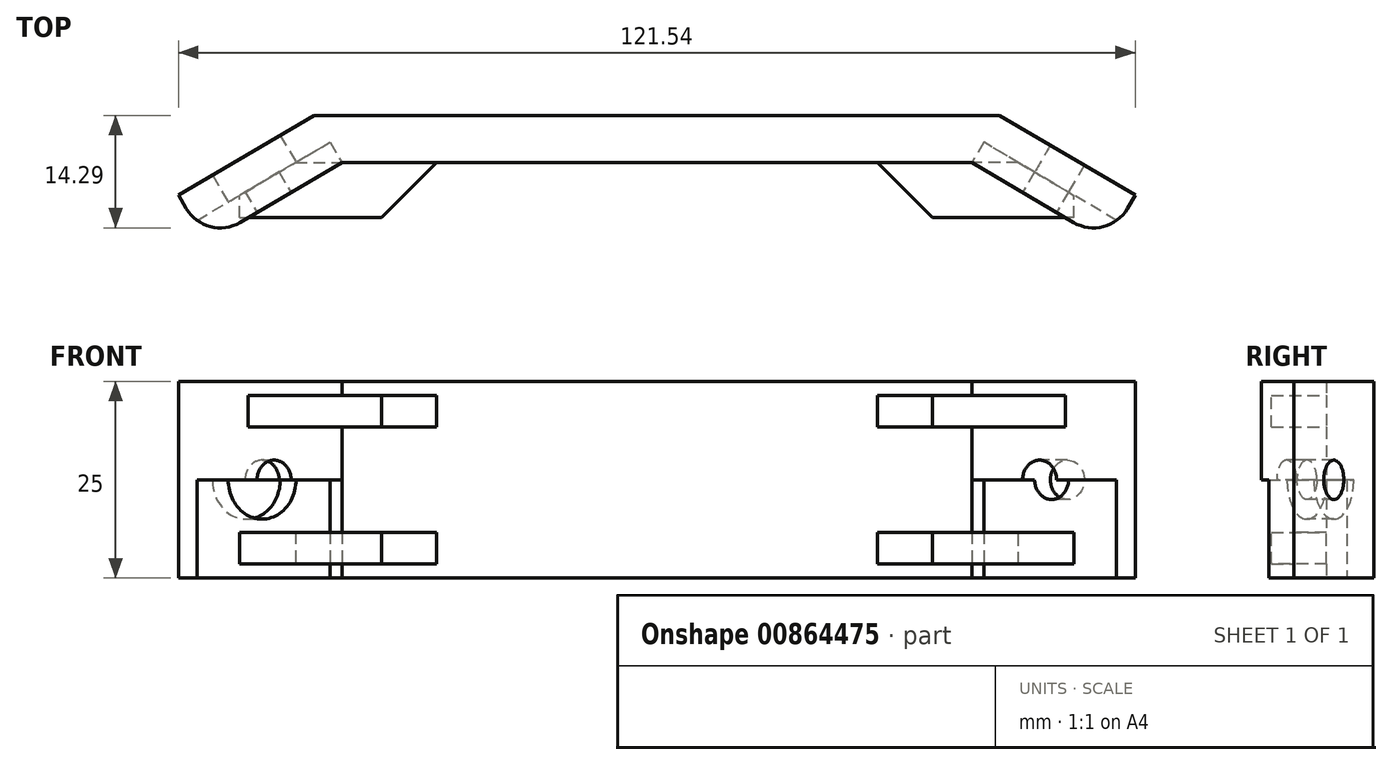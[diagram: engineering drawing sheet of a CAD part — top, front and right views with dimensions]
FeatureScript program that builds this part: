
annotation { "Feature Type Name" : "Feature", "Feature Type Description" : "" }
export const myFeature = defineFeature(function(context is Context, id is Id, definition is map)
    precondition{}
    {
        {
            var Q0;
            Q0=qCreatedBy(makeId("Top.planeOp"),FACE);
            var sketch = newSketch(context, id + "F0", { "sketchPlane" : qUnion([Q0])});
            skLineSegment(sketch, "E0", {"start": v(-33.18, 0) * mm, "end": v(46.82, 0) * mm});
            skLineSegment(sketch, "E1", {"start": v(46.82, 0) * mm, "end": v(46.82, -6) * mm});
            skLineSegment(sketch, "E2", {"start": v(46.82, -6) * mm, "end": v(-33.18, -6) * mm});
            skLineSegment(sketch, "E3", {"start": v(-33.18, -6) * mm, "end": v(-33.18, 0) * mm});
            skLineSegment(sketch, "E4", {"start": v(-33.18, -6) * mm, "end": v(-36.7, 0) * mm});
            skLineSegment(sketch, "E5", {"start": v(-33.18, 0) * mm, "end": v(-36.7, 0) * mm});
            skLineSegment(sketch, "E6", {"start": v(46.82, 0) * mm, "end": v(50.35, 0) * mm});
            skLineSegment(sketch, "E7", {"start": v(50.35, 0) * mm, "end": v(46.82, -6) * mm});
            skLineSegment(sketch, "E8", {"start": v(-36.7, 0) * mm, "end": v(-53.95, -10.14) * mm});
            skLineSegment(sketch, "E9", {"start": v(-53.95, -10.14) * mm, "end": v(-50.42, -16.14) * mm});
            skLineSegment(sketch, "E10", {"start": v(-50.42, -16.14) * mm, "end": v(-33.18, -6) * mm});
            skLineSegment(sketch, "E11", {"start": v(-33.18, 0) * mm, "end": v(6.82, 0) * mm});
            skLineSegment(sketch, "E12", {"start": v(50.35, 0) * mm, "end": v(67.59, -10.14) * mm});
            skLineSegment(sketch, "E13", {"start": v(67.59, -10.14) * mm, "end": v(64.06, -16.14) * mm});
            skLineSegment(sketch, "E14", {"start": v(64.06, -16.14) * mm, "end": v(46.82, -6) * mm});
            skSolve(sketch);
        }
        {
            var Q0;
            Q0=makeQuery(id+"F0.imprint","IMPRINT",FACE,{"disambiguationData":[TD([[makeQuery(id+"F0.imprint","IMPRINT",EDGE,{"derivedFrom":sQuery(id+"F0.wireOp",EDGE,"E4")}),1.0]])]});
            var Q1;
            Q1=makeQuery(id+"F0.imprint","IMPRINT",FACE,{"disambiguationData":[TD([[makeQuery(id+"F0.imprint","IMPRINT",EDGE,{"derivedFrom":sQuery(id+"F0.wireOp",EDGE,"E3")}),1.0]])]});
            var Q2;
            Q2=makeQuery(id+"F0.imprint","IMPRINT",FACE,{"disambiguationData":[TD([[makeQuery(id+"F0.imprint","IMPRINT",EDGE,{"derivedFrom":sQuery(id+"F0.wireOp",EDGE,"E0")}),-1.0]])]});
            var Q3;
            Q3=makeQuery(id+"F0.imprint","IMPRINT",FACE,{"disambiguationData":[TD([[makeQuery(id+"F0.imprint","IMPRINT",EDGE,{"derivedFrom":sQuery(id+"F0.wireOp",EDGE,"E1")}),1.0]])]});
            var Q4;
            Q4=makeQuery(id+"F0.imprint","IMPRINT",FACE,{"disambiguationData":[TD([[makeQuery(id+"F0.imprint","IMPRINT",EDGE,{"derivedFrom":sQuery(id+"F0.wireOp",EDGE,"E7")}),1.0]])]});
            extrude(context, id + "F1", {"entities" : qUnion([Q0, Q1, Q2, Q3, Q4]), "depth" : 25 * mm, "offsetDistance" : 25 * mm});
        }
        {
            var Q0;
            Q0=makeQuery(id+"F1.opExtrude","SWEPT_FACE",FACE,{"disambiguationData":[OSD([sQuery(id+"F0.wireOp",EDGE,"E10")])]});
            var sketch = newSketch(context, id + "F2", { "sketchPlane" : qUnion([Q0])});
            skLineSegment(sketch, "E15", {"start": v(-41.65, 25) * mm, "end": v(-41.65, 0) * mm});
            skLineSegment(sketch, "E16", {"start": v(-51.65, 12.5) * mm, "end": v(-31.65, 12.5) * mm});
            skCircle(sketch, "E17", {"center": v(-41.65, 12.5) * mm, "radius": 5 * mm});
            skCircle(sketch, "E18", {"center": v(-41.65, 12.5) * mm, "radius": 2.5 * mm});
            skSolve(sketch);
        }
        {
            var Q0;
            {var subQ0=sQuery(id+"F2.wireOp",EDGE,"E16");var subQ1=sQuery(id+"F2.wireOp",EDGE,"E15");var subQ2=makeQuery(id+"F2.imprint","INTERSECT",VERTEX,{"derivedFrom":[subQ1,subQ0]});Q0=makeQuery(id+"F2.imprint","IMPRINT",FACE,{"disambiguationData":[TD([[makeQuery(id+"F2.imprint","IMPRINT",EDGE,{"disambiguationData":[TD([[subQ2,-1.0]])],"derivedFrom":subQ1}),-1.0]])]});}
            var Q1;
            {var subQ0=sQuery(id+"F2.wireOp",EDGE,"E16");var subQ1=sQuery(id+"F2.wireOp",EDGE,"E15");var subQ2=makeQuery(id+"F2.imprint","INTERSECT",VERTEX,{"derivedFrom":[subQ1,subQ0]});Q1=makeQuery(id+"F2.imprint","IMPRINT",FACE,{"disambiguationData":[TD([[makeQuery(id+"F2.imprint","IMPRINT",EDGE,{"disambiguationData":[TD([[subQ2,-1.0]])],"derivedFrom":subQ1}),1.0]])]});}
            var Q2;
            {var subQ0=sQuery(id+"F2.wireOp",EDGE,"E18");var subQ1=sQuery(id+"F2.wireOp",EDGE,"E15");var subQ2=makeQuery(id+"F2.imprint","INTERSECT",VERTEX,{"disambiguationData":[OD(0.0)],"derivedFrom":[subQ1,subQ0]});Q2=makeQuery(id+"F2.imprint","IMPRINT",FACE,{"disambiguationData":[TD([[makeQuery(id+"F2.imprint","IMPRINT",EDGE,{"disambiguationData":[TD([[subQ2,-1.0]])],"derivedFrom":subQ1}),1.0]])]});}
            var Q3;
            {var subQ0=sQuery(id+"F2.wireOp",EDGE,"E18");var subQ1=sQuery(id+"F2.wireOp",EDGE,"E15");var subQ2=makeQuery(id+"F2.imprint","INTERSECT",VERTEX,{"disambiguationData":[OD(0.0)],"derivedFrom":[subQ1,subQ0]});Q3=makeQuery(id+"F2.imprint","IMPRINT",FACE,{"disambiguationData":[TD([[makeQuery(id+"F2.imprint","IMPRINT",EDGE,{"disambiguationData":[TD([[subQ2,-1.0]])],"derivedFrom":subQ1}),-1.0]])]});}
            extrude(context, id + "F3", {"entities" : qUnion([Q0, Q1, Q2, Q3]), "operationType" : NewBodyOperationType.REMOVE, "oppositeDirection" : true, "depth" : 25 * mm, "offsetDistance" : 25 * mm});
        }
        {
            var Q0;
            {var subQ0=sQuery(id+"F2.wireOp",EDGE,"E17");var subQ1=sQuery(id+"F2.wireOp",EDGE,"E15");var subQ2=makeQuery(id+"F2.imprint","INTERSECT",VERTEX,{"disambiguationData":[OD(0.0)],"derivedFrom":[subQ1,subQ0]});Q0=makeQuery(id+"F2.imprint","IMPRINT",FACE,{"disambiguationData":[TD([[makeQuery(id+"F2.imprint","IMPRINT",EDGE,{"disambiguationData":[TD([[subQ2,-1.0]])],"derivedFrom":subQ1}),-1.0]])]});}
            var Q1;
            {var subQ0=sQuery(id+"F2.wireOp",EDGE,"E18");var subQ1=sQuery(id+"F2.wireOp",EDGE,"E15");var subQ2=makeQuery(id+"F2.imprint","INTERSECT",VERTEX,{"disambiguationData":[OD(1.0)],"derivedFrom":[subQ1,subQ0]});Q1=makeQuery(id+"F2.imprint","IMPRINT",FACE,{"disambiguationData":[TD([[makeQuery(id+"F2.imprint","IMPRINT",EDGE,{"disambiguationData":[TD([[subQ2,-1.0]])],"derivedFrom":subQ1}),-1.0]])]});}
            var Q2;
            {var subQ0=sQuery(id+"F2.wireOp",EDGE,"E18");var subQ1=sQuery(id+"F2.wireOp",EDGE,"E15");var subQ2=makeQuery(id+"F2.imprint","INTERSECT",VERTEX,{"disambiguationData":[OD(1.0)],"derivedFrom":[subQ1,subQ0]});Q2=makeQuery(id+"F2.imprint","IMPRINT",FACE,{"disambiguationData":[TD([[makeQuery(id+"F2.imprint","IMPRINT",EDGE,{"disambiguationData":[TD([[subQ2,-1.0]])],"derivedFrom":subQ1}),1.0]])]});}
            var Q3;
            {var subQ0=sQuery(id+"F2.wireOp",EDGE,"E17");var subQ1=sQuery(id+"F2.wireOp",EDGE,"E15");var subQ2=makeQuery(id+"F2.imprint","INTERSECT",VERTEX,{"disambiguationData":[OD(0.0)],"derivedFrom":[subQ1,subQ0]});Q3=makeQuery(id+"F2.imprint","IMPRINT",FACE,{"disambiguationData":[TD([[makeQuery(id+"F2.imprint","IMPRINT",EDGE,{"disambiguationData":[TD([[subQ2,-1.0]])],"derivedFrom":subQ1}),1.0]])]});}
            extrude(context, id + "F4", {"entities" : qUnion([Q0, Q1, Q2, Q3]), "operationType" : NewBodyOperationType.REMOVE, "oppositeDirection" : true, "depth" : 3 * mm, "offsetDistance" : 25 * mm});
        }
        {
            var Q0;
            Q0=makeQuery(id+"F1.opExtrude","SWEPT_FACE",FACE,{"disambiguationData":[OSD([sQuery(id+"F0.wireOp",EDGE,"E14")])]});
            var sketch = newSketch(context, id + "F5", { "sketchPlane" : qUnion([Q0])});
            skLineSegment(sketch, "E19", {"start": v(53.4, 25) * mm, "end": v(53.4, 0) * mm});
            skLineSegment(sketch, "E20", {"start": v(63.4, 12.5) * mm, "end": v(43.4, 12.5) * mm});
            skCircle(sketch, "E21", {"center": v(53.4, 12.5) * mm, "radius": 5 * mm});
            skCircle(sketch, "E22", {"center": v(53.4, 12.5) * mm, "radius": 2.5 * mm});
            skSolve(sketch);
        }
        {
            var Q0;
            {var subQ0=sQuery(id+"F5.wireOp",EDGE,"E20");var subQ1=sQuery(id+"F5.wireOp",EDGE,"E19");var subQ2=makeQuery(id+"F5.imprint","INTERSECT",VERTEX,{"derivedFrom":[subQ1,subQ0]});Q0=makeQuery(id+"F5.imprint","IMPRINT",FACE,{"disambiguationData":[TD([[makeQuery(id+"F5.imprint","IMPRINT",EDGE,{"disambiguationData":[TD([[subQ2,-1.0]])],"derivedFrom":subQ1}),1.0]])]});}
            var Q1;
            {var subQ0=sQuery(id+"F5.wireOp",EDGE,"E20");var subQ1=sQuery(id+"F5.wireOp",EDGE,"E19");var subQ2=makeQuery(id+"F5.imprint","INTERSECT",VERTEX,{"derivedFrom":[subQ1,subQ0]});Q1=makeQuery(id+"F5.imprint","IMPRINT",FACE,{"disambiguationData":[TD([[makeQuery(id+"F5.imprint","IMPRINT",EDGE,{"disambiguationData":[TD([[subQ2,-1.0]])],"derivedFrom":subQ1}),-1.0]])]});}
            var Q2;
            {var subQ0=sQuery(id+"F5.wireOp",EDGE,"E22");var subQ1=sQuery(id+"F5.wireOp",EDGE,"E19");var subQ2=makeQuery(id+"F5.imprint","INTERSECT",VERTEX,{"disambiguationData":[OD(0.0)],"derivedFrom":[subQ1,subQ0]});Q2=makeQuery(id+"F5.imprint","IMPRINT",FACE,{"disambiguationData":[TD([[makeQuery(id+"F5.imprint","IMPRINT",EDGE,{"disambiguationData":[TD([[subQ2,-1.0]])],"derivedFrom":subQ1}),-1.0]])]});}
            var Q3;
            {var subQ0=sQuery(id+"F5.wireOp",EDGE,"E22");var subQ1=sQuery(id+"F5.wireOp",EDGE,"E19");var subQ2=makeQuery(id+"F5.imprint","INTERSECT",VERTEX,{"disambiguationData":[OD(0.0)],"derivedFrom":[subQ1,subQ0]});Q3=makeQuery(id+"F5.imprint","IMPRINT",FACE,{"disambiguationData":[TD([[makeQuery(id+"F5.imprint","IMPRINT",EDGE,{"disambiguationData":[TD([[subQ2,-1.0]])],"derivedFrom":subQ1}),1.0]])]});}
            extrude(context, id + "F6", {"entities" : qUnion([Q0, Q1, Q2, Q3]), "operationType" : NewBodyOperationType.REMOVE, "oppositeDirection" : true, "depth" : 25 * mm, "offsetDistance" : 25 * mm});
        }
        {
            var Q0;
            {var subQ0=sQuery(id+"F5.wireOp",EDGE,"E22");var subQ1=sQuery(id+"F5.wireOp",EDGE,"E19");var subQ2=makeQuery(id+"F5.imprint","INTERSECT",VERTEX,{"disambiguationData":[OD(1.0)],"derivedFrom":[subQ1,subQ0]});Q0=makeQuery(id+"F5.imprint","IMPRINT",FACE,{"disambiguationData":[TD([[makeQuery(id+"F5.imprint","IMPRINT",EDGE,{"disambiguationData":[TD([[subQ2,-1.0]])],"derivedFrom":subQ1}),1.0]])]});}
            var Q1;
            {var subQ0=sQuery(id+"F5.wireOp",EDGE,"E22");var subQ1=sQuery(id+"F5.wireOp",EDGE,"E19");var subQ2=makeQuery(id+"F5.imprint","INTERSECT",VERTEX,{"disambiguationData":[OD(1.0)],"derivedFrom":[subQ1,subQ0]});Q1=makeQuery(id+"F5.imprint","IMPRINT",FACE,{"disambiguationData":[TD([[makeQuery(id+"F5.imprint","IMPRINT",EDGE,{"disambiguationData":[TD([[subQ2,-1.0]])],"derivedFrom":subQ1}),-1.0]])]});}
            var Q2;
            {var subQ0=sQuery(id+"F5.wireOp",EDGE,"E21");var subQ1=sQuery(id+"F5.wireOp",EDGE,"E19");var subQ2=makeQuery(id+"F5.imprint","INTERSECT",VERTEX,{"disambiguationData":[OD(0.0)],"derivedFrom":[subQ1,subQ0]});Q2=makeQuery(id+"F5.imprint","IMPRINT",FACE,{"disambiguationData":[TD([[makeQuery(id+"F5.imprint","IMPRINT",EDGE,{"disambiguationData":[TD([[subQ2,-1.0]])],"derivedFrom":subQ1}),-1.0]])]});}
            var Q3;
            {var subQ0=sQuery(id+"F5.wireOp",EDGE,"E21");var subQ1=sQuery(id+"F5.wireOp",EDGE,"E19");var subQ2=makeQuery(id+"F5.imprint","INTERSECT",VERTEX,{"disambiguationData":[OD(0.0)],"derivedFrom":[subQ1,subQ0]});Q3=makeQuery(id+"F5.imprint","IMPRINT",FACE,{"disambiguationData":[TD([[makeQuery(id+"F5.imprint","IMPRINT",EDGE,{"disambiguationData":[TD([[subQ2,-1.0]])],"derivedFrom":subQ1}),1.0]])]});}
            extrude(context, id + "F7", {"entities" : qUnion([Q0, Q1, Q2, Q3]), "operationType" : NewBodyOperationType.REMOVE, "oppositeDirection" : true, "depth" : 3 * mm, "offsetDistance" : 25 * mm});
        }
        {
            var Q0;
            Q0=makeQuery(id+"F1.opExtrude","SWEPT_EDGE",EDGE,{"disambiguationData":[OSD([sQuery(id+"F0.wireOp",EDGE,"E13"),sQuery(id+"F0.wireOp",EDGE,"E14")])]});
            fillet(context, id + "F8", {"entities" : qUnion([Q0]), "radius" : 5 * mm, "tangentPropagation" : true, "allowEdgeOverflow" : false});
        }
        {
            var Q0;
            Q0=makeQuery(id+"F1.opExtrude","SWEPT_EDGE",EDGE,{"disambiguationData":[OSD([sQuery(id+"F0.wireOp",EDGE,"E9"),sQuery(id+"F0.wireOp",EDGE,"E10")])]});
            fillet(context, id + "F9", {"entities" : qUnion([Q0]), "radius" : 5 * mm, "tangentPropagation" : true, "allowEdgeOverflow" : false});
        }
        {
            var Q0;
            Q0=makeQuery(id+"F1.opExtrude","SWEPT_FACE",FACE,{"disambiguationData":[OSD([sQuery(id+"F0.wireOp",EDGE,"E2")])]});
            var sketch = newSketch(context, id + "F10", { "sketchPlane" : qUnion([Q0])});
            skLineSegment(sketch, "E23.bottom", {"start": v(-46.18, 1.82) * mm, "end": v(-21.18, 1.82) * mm});
            skLineSegment(sketch, "E23.top", {"start": v(-46.18, 5.82) * mm, "end": v(-21.18, 5.82) * mm});
            skLineSegment(sketch, "E23.left", {"start": v(-46.18, 1.82) * mm, "end": v(-46.18, 5.82) * mm});
            skLineSegment(sketch, "E23.right", {"start": v(-21.18, 1.82) * mm, "end": v(-21.18, 5.82) * mm});
            skLineSegment(sketch, "E24.MirrorCS", {"start": v(-46.18, 19.18) * mm, "end": v(-21.18, 19.18) * mm});
            skLineSegment(sketch, "E25.MirrorCS", {"start": v(-21.18, 23.18) * mm, "end": v(-21.18, 19.18) * mm});
            skLineSegment(sketch, "E26.MirrorCS", {"start": v(-46.18, 23.18) * mm, "end": v(-46.18, 19.18) * mm});
            skLineSegment(sketch, "E27.MirrorCS", {"start": v(-46.18, 23.18) * mm, "end": v(-21.18, 23.18) * mm});
            skLineSegment(sketch, "E28.MirrorCS", {"start": v(34.82, 1.82) * mm, "end": v(34.82, 5.82) * mm});
            skLineSegment(sketch, "E29.MirrorCS", {"start": v(34.82, 23.18) * mm, "end": v(34.82, 19.18) * mm});
            skLineSegment(sketch, "E30.MirrorCS", {"start": v(59.82, 1.82) * mm, "end": v(59.82, 5.82) * mm});
            skLineSegment(sketch, "E31.MirrorCS", {"start": v(59.82, 23.18) * mm, "end": v(59.82, 19.18) * mm});
            skLineSegment(sketch, "E32.MirrorCS", {"start": v(59.82, 1.82) * mm, "end": v(34.82, 1.82) * mm});
            skLineSegment(sketch, "E33.MirrorCS", {"start": v(59.82, 5.82) * mm, "end": v(34.82, 5.82) * mm});
            skLineSegment(sketch, "E34.MirrorCS", {"start": v(59.82, 23.18) * mm, "end": v(34.82, 23.18) * mm});
            skLineSegment(sketch, "E35.MirrorCS", {"start": v(59.82, 19.18) * mm, "end": v(34.82, 19.18) * mm});
            skSolve(sketch);
        }
        {
            var Q0;
            {var subQ0=sQuery(id+"F10.wireOp",EDGE,"E25.MirrorCS");Q0=makeQuery(id+"F10.imprint","IMPRINT",FACE,{"disambiguationData":[TD([[makeQuery(id+"F10.imprint","IMPRINT",EDGE,{"derivedFrom":subQ0}),-1.0]])]});}
            var Q1;
            {var subQ0=sQuery(id+"F10.wireOp",EDGE,"E26.MirrorCS");Q1=makeQuery(id+"F10.imprint","IMPRINT",FACE,{"disambiguationData":[TD([[makeQuery(id+"F10.imprint","IMPRINT",EDGE,{"derivedFrom":subQ0}),1.0]])]});}
            var Q2;
            {var subQ0=sQuery(id+"F10.wireOp",EDGE,"E23.right");Q2=makeQuery(id+"F10.imprint","IMPRINT",FACE,{"disambiguationData":[TD([[makeQuery(id+"F10.imprint","IMPRINT",EDGE,{"derivedFrom":subQ0}),1.0]])]});}
            var Q3;
            {var subQ0=sQuery(id+"F10.wireOp",EDGE,"E23.left");Q3=makeQuery(id+"F10.imprint","IMPRINT",FACE,{"disambiguationData":[TD([[makeQuery(id+"F10.imprint","IMPRINT",EDGE,{"derivedFrom":subQ0}),-1.0]])]});}
            var Q4;
            {var subQ0=sQuery(id+"F10.wireOp",EDGE,"E29.MirrorCS");Q4=makeQuery(id+"F10.imprint","IMPRINT",FACE,{"disambiguationData":[TD([[makeQuery(id+"F10.imprint","IMPRINT",EDGE,{"derivedFrom":subQ0}),1.0]])]});}
            var Q5;
            {var subQ0=sQuery(id+"F10.wireOp",EDGE,"E31.MirrorCS");Q5=makeQuery(id+"F10.imprint","IMPRINT",FACE,{"disambiguationData":[TD([[makeQuery(id+"F10.imprint","IMPRINT",EDGE,{"derivedFrom":subQ0}),-1.0]])]});}
            var Q6;
            {var subQ0=sQuery(id+"F10.wireOp",EDGE,"E30.MirrorCS");Q6=makeQuery(id+"F10.imprint","IMPRINT",FACE,{"disambiguationData":[TD([[makeQuery(id+"F10.imprint","IMPRINT",EDGE,{"derivedFrom":subQ0}),1.0]])]});}
            var Q7;
            {var subQ0=sQuery(id+"F10.wireOp",EDGE,"E28.MirrorCS");Q7=makeQuery(id+"F10.imprint","IMPRINT",FACE,{"disambiguationData":[TD([[makeQuery(id+"F10.imprint","IMPRINT",EDGE,{"derivedFrom":subQ0}),-1.0]])]});}
            extrude(context, id + "F11", {"entities" : qUnion([Q0, Q1, Q2, Q3, Q4, Q5, Q6, Q7]), "operationType" : NewBodyOperationType.ADD, "depth" : 7 * mm, "offsetDistance" : 25 * mm});
        }
        {
            var Q0;
            Q0=makeQuery(id+"F11.opExtrude","CAP_EDGE",EDGE,{"disambiguationData":[OSD([sQuery(id+"F10.wireOp",EDGE,"E23.right")])],"isStart":false});
            var Q1;
            Q1=makeQuery(id+"F11.opExtrude","CAP_EDGE",EDGE,{"disambiguationData":[OSD([sQuery(id+"F10.wireOp",EDGE,"E25.MirrorCS")])],"isStart":false});
            var Q2;
            Q2=makeQuery(id+"F11.opExtrude","CAP_EDGE",EDGE,{"disambiguationData":[OSD([sQuery(id+"F10.wireOp",EDGE,"E29.MirrorCS")])],"isStart":false});
            var Q3;
            Q3=makeQuery(id+"F11.opExtrude","CAP_EDGE",EDGE,{"disambiguationData":[OSD([sQuery(id+"F10.wireOp",EDGE,"E28.MirrorCS")])],"isStart":false});
            chamfer(context, id + "F12", {"entities" : qUnion([Q0, Q1, Q2, Q3]), "width" : 7 * mm, "tangentPropagation" : true});
        }
    });
